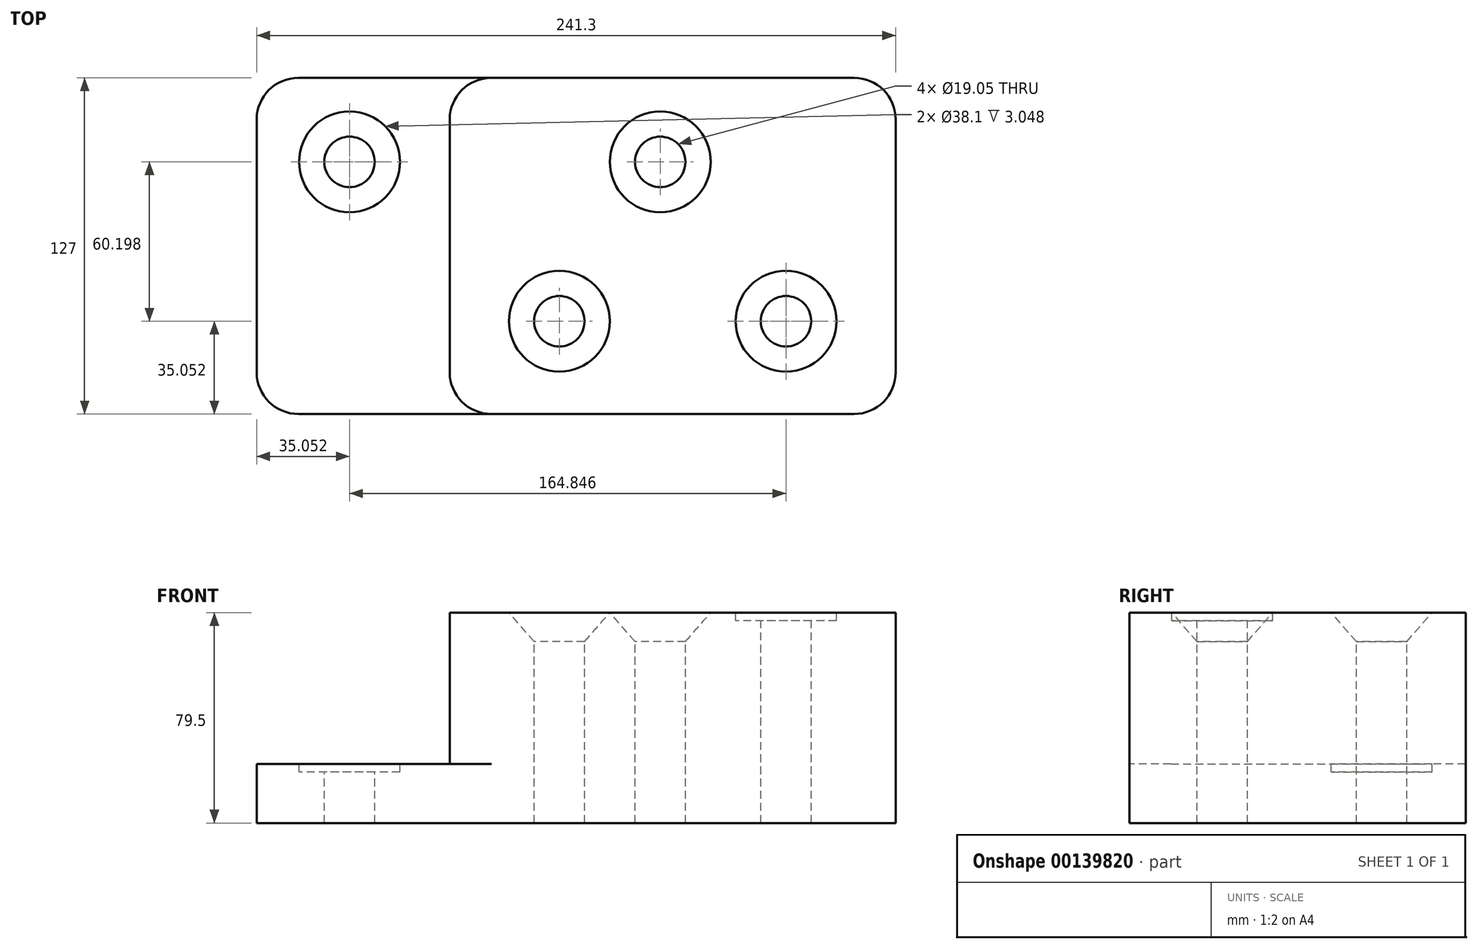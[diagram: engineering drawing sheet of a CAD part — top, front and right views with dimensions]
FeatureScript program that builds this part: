
annotation { "Feature Type Name" : "Feature", "Feature Type Description" : "" }
export const myFeature = defineFeature(function(context is Context, id is Id, definition is map)
    precondition{}
    {
        {
            var Q0;
            Q0=qCreatedBy(makeId("Top.planeOp"),FACE);
            var sketch = newSketch(context, id + "F0", { "sketchPlane" : qUnion([Q0])});
            skLineSegment(sketch, "E0.bottom", {"start": v(15.75, 0) * mm, "end": v(225.55, 0) * mm});
            skLineSegment(sketch, "E0.top", {"start": v(15.75, 127) * mm, "end": v(225.55, 127) * mm});
            skLineSegment(sketch, "E0.left", {"start": v(0, 15.75) * mm, "end": v(0, 111.25) * mm});
            skLineSegment(sketch, "E0.right", {"start": v(241.3, 15.75) * mm, "end": v(241.3, 111.25) * mm});
            skLineSegment(sketch, "E1", {"start": v(72.9, 127) * mm, "end": v(72.9, 0) * mm});
            skPoint(sketch, "E2.visualSharp", {"position": v(0, 127) * mm});
            skArc(sketch, "E2.filletArc", {"start": v(15.75, 127) * mm, "mid": v(4.61, 122.39) * mm, "end": v(0, 111.25) * mm});
            skPoint(sketch, "E3.visualSharp", {"position": v(0, 0) * mm});
            skArc(sketch, "E3.filletArc", {"start": v(0, 15.75) * mm, "mid": v(4.61, 4.61) * mm, "end": v(15.75, 0) * mm});
            skPoint(sketch, "E4.visualSharp", {"position": v(241.3, 0) * mm});
            skArc(sketch, "E4.filletArc", {"start": v(225.55, 0) * mm, "mid": v(236.69, 4.61) * mm, "end": v(241.3, 15.75) * mm});
            skPoint(sketch, "E5.visualSharp", {"position": v(241.3, 127) * mm});
            skArc(sketch, "E5.filletArc", {"start": v(241.3, 111.25) * mm, "mid": v(236.69, 122.39) * mm, "end": v(225.55, 127) * mm});
            skSolve(sketch);
        }
        {
            var Q0;
            Q0 = qSketchRegion(id + "F0", true);
            extrude(context, id + "F1", {"entities" : qUnion([Q0]), "depth" : 22.35 * mm});
        }
        {
            var Q0;
            Q0=makeQuery(id+"F0.imprint","IMPRINT",FACE,{"disambiguationData":[TD([[makeQuery(id+"F0.imprint","IMPRINT",EDGE,{"derivedFrom":sQuery(id+"F0.wireOp",EDGE,"E0.right")}),1.0]])]});
            extrude(context, id + "F2", {"entities" : qUnion([Q0]), "operationType" : NewBodyOperationType.ADD, "depth" : 79.5 * mm});
        }
        {
            var Q0;
            Q0=makeQuery(id+"F2.opExtrude","SWEPT_EDGE",EDGE,{"disambiguationData":[OSD([sQuery(id+"F0.wireOp",EDGE,"E0.bottom"),sQuery(id+"F0.wireOp",EDGE,"E1")])]});
            var Q1;
            Q1=makeQuery(id+"F2.opExtrude","SWEPT_EDGE",EDGE,{"disambiguationData":[OSD([sQuery(id+"F0.wireOp",EDGE,"E0.top"),sQuery(id+"F0.wireOp",EDGE,"E1")])]});
            fillet(context, id + "F3", {"entities" : qUnion([Q0, Q1]), "radius" : 15.75 * mm, "tangentPropagation" : true, "allowEdgeOverflow" : false});
        }
        {
            var Q0;
            Q0=makeQuery(id+"F2.opExtrude","CAP_FACE",FACE,{"disambiguationData":[OSD([sQuery(id+"F0.wireOp",EDGE,"E0.bottom"),sQuery(id+"F0.wireOp",EDGE,"E0.top"),sQuery(id+"F0.wireOp",EDGE,"E0.right"),sQuery(id+"F0.wireOp",EDGE,"E1"),sQuery(id+"F0.wireOp",EDGE,"E4.filletArc"),sQuery(id+"F0.wireOp",EDGE,"E5.filletArc")])],"isStart":false});
            var sketch = newSketch(context, id + "F4", { "sketchPlane" : qUnion([Q0])});
            skPoint(sketch, "E6", {"position": v(35.05, 95.25) * mm});
            skPoint(sketch, "E7", {"position": v(114.3, 35.05) * mm});
            skPoint(sketch, "E8", {"position": v(199.9, 35.05) * mm});
            skPoint(sketch, "E9", {"position": v(152.4, 95.25) * mm});
            skSolve(sketch);
        }
        {
            var Q0;
            Q0=sQuery(id+"F4.wireOp",VERTEX,"E9");
            var Q1;
            Q1=sQuery(id+"F4.wireOp",VERTEX,"E7");
            var Q2;
            Q2=makeQuery(id+"F1.opExtrude","SWEPT_BODY",BODY,{"disambiguationData":[OSD([sQuery(id+"F0.wireOp",EDGE,"E0.bottom"),sQuery(id+"F0.wireOp",EDGE,"E0.top"),sQuery(id+"F0.wireOp",EDGE,"E0.left"),sQuery(id+"F0.wireOp",EDGE,"E0.right"),sQuery(id+"F0.wireOp",EDGE,"E2.filletArc"),sQuery(id+"F0.wireOp",EDGE,"E3.filletArc"),sQuery(id+"F0.wireOp",EDGE,"E4.filletArc"),sQuery(id+"F0.wireOp",EDGE,"E5.filletArc")])]});
            hole(context, id + "F5", {"style" : HoleStyle.C_SINK, "endStyle" : HoleEndStyle.THROUGH, "holeDiameter" : 19.05 * mm, "cSinkDiameter" : 38.1 * mm, "cSinkAngle" : 82 * degree, "locations" : qUnion([Q0, Q1]), "scope" : qUnion([Q2]), "isTappedThrough" : true});
        }
        {
            var Q0;
            Q0=sQuery(id+"F4.wireOp",VERTEX,"E8");
            var Q1;
            Q1=sQuery(id+"F4.wireOp",VERTEX,"E6");
            var Q2;
            Q2=makeQuery(id+"F1.opExtrude","SWEPT_BODY",BODY,{"disambiguationData":[OSD([sQuery(id+"F0.wireOp",EDGE,"E0.bottom"),sQuery(id+"F0.wireOp",EDGE,"E0.top"),sQuery(id+"F0.wireOp",EDGE,"E0.left"),sQuery(id+"F0.wireOp",EDGE,"E0.right"),sQuery(id+"F0.wireOp",EDGE,"E2.filletArc"),sQuery(id+"F0.wireOp",EDGE,"E3.filletArc"),sQuery(id+"F0.wireOp",EDGE,"E4.filletArc"),sQuery(id+"F0.wireOp",EDGE,"E5.filletArc")])]});
            hole(context, id + "F6", {"style" : HoleStyle.C_BORE, "endStyle" : HoleEndStyle.THROUGH, "holeDiameter" : 19.05 * mm, "cBoreDiameter" : 38.1 * mm, "cBoreDepth" : 3.05 * mm, "locations" : qUnion([Q0, Q1]), "scope" : qUnion([Q2]), "isTappedThrough" : true});
        }
    });
